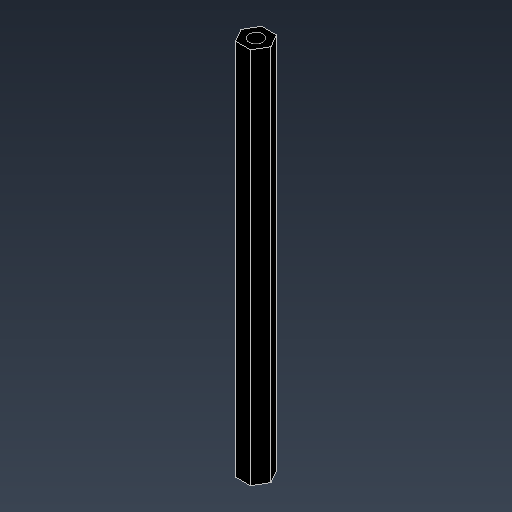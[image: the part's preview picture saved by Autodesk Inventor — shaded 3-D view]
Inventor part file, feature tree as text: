
AUTODESK INVENTOR PART (.ipt)
format: ipt  version: 2024.1 (Build 281209000, 209)  size: 98,816 bytes
history: native  units: mm
features: extrude x1, sketch x1
ambient origin geometry x8: Origin, YZ Plane, XZ Plane, XY Plane, X Axis, Y Axis, Z Axis, Center Point
bodies: Solid1 (feature_tree)
feature tree (2):
  extrude  "Extrusion1"  Depth=80.0mm
  sketch  "Sketch1"  dims[d0=5.5mm d1=3.0mm d2=80.0mm d3=0.0mm d4=0.5mm d5=0.872665mm]
